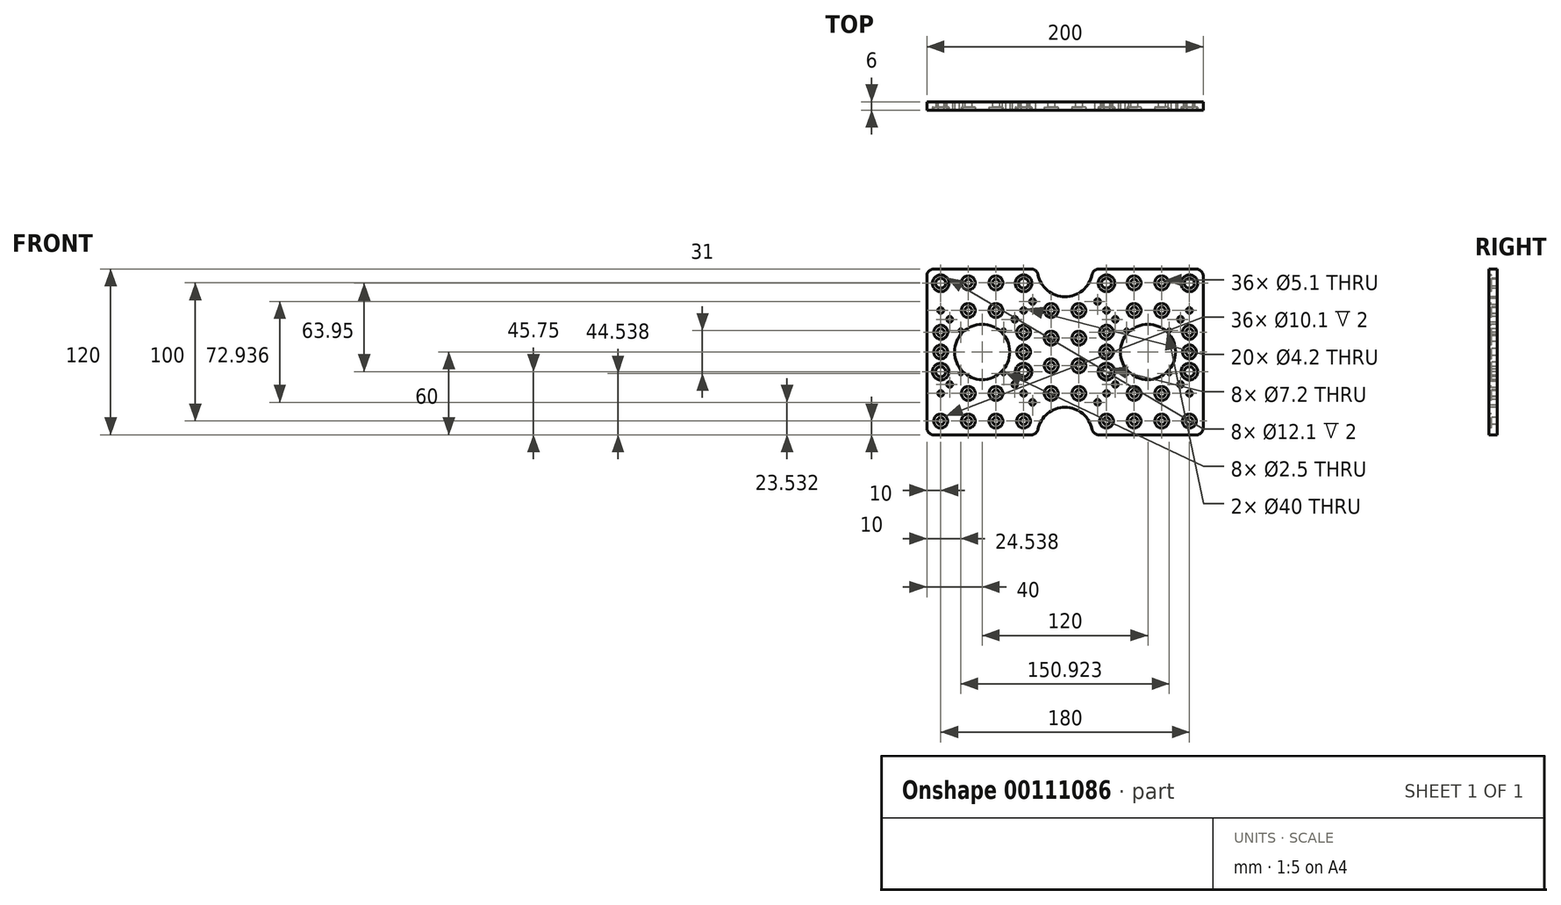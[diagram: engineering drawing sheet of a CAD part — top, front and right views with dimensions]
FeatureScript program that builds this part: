
annotation { "Feature Type Name" : "Feature", "Feature Type Description" : "" }
export const myFeature = defineFeature(function(context is Context, id is Id, definition is map)
    precondition{}
    {
        {
            var Q0;
            Q0=qCreatedBy(makeId("Front.planeOp"),FACE);
            var sketch = newSketch(context, id + "F0", { "sketchPlane" : qUnion([Q0])});
            skPoint(sketch, "E0", {"position": v(10, 10) * mm});
            skPoint(sketch, "E1.0.1.0", {"position": v(10, 30) * mm});
            skPoint(sketch, "E1.1.0.0", {"position": v(30, 10) * mm});
            skPoint(sketch, "E1.1.1.0", {"position": v(30, 30) * mm});
            skPoint(sketch, "E1.2.0.0", {"position": v(50, 10) * mm});
            skPoint(sketch, "E1.2.1.0", {"position": v(50, 30) * mm});
            skPoint(sketch, "E1.3.0.0", {"position": v(70, 10) * mm});
            skPoint(sketch, "E1.3.1.0", {"position": v(70, 30) * mm});
            skLineSegment(sketch, "E1.direction1", {"start": v(10, 10) * mm, "end": v(30, 10) * mm, "construction": true});
            skLineSegment(sketch, "E1.direction2", {"start": v(10, 10) * mm, "end": v(10, 30) * mm, "construction": true});
            skLineSegment(sketch, "E2.bottom", {"start": v(5, 0) * mm, "end": v(75.5, 0) * mm});
            skLineSegment(sketch, "E2.top", {"start": v(5, 120) * mm, "end": v(75.5, 120) * mm});
            skLineSegment(sketch, "E2.left", {"start": v(0, 5) * mm, "end": v(0, 115) * mm});
            skLineSegment(sketch, "E2.right", {"start": v(100, 20) * mm, "end": v(100, 100) * mm});
            skArc(sketch, "E3", {"start": v(80.4, 116) * mm, "mid": v(87.35, 104.5) * mm, "end": v(100, 100) * mm});
            skArc(sketch, "E4", {"start": v(100, 20) * mm, "mid": v(87.35, 15.5) * mm, "end": v(80.4, 4) * mm});
            skCircle(sketch, "E5", {"center": v(40, 60) * mm, "radius": 20 * mm});
            skPoint(sketch, "E5.centerSnap0", {"position": v(0, 60) * mm});
            skPoint(sketch, "E6", {"position": v(10, 60) * mm});
            skPoint(sketch, "E7", {"position": v(70, 60) * mm});
            skPoint(sketch, "E8.0.0.4", {"position": v(10, 90) * mm});
            skPoint(sketch, "E8.0.1.4", {"position": v(30, 90) * mm});
            skPoint(sketch, "E8.0.1.5", {"position": v(30, 110) * mm});
            skPoint(sketch, "E8.0.2.4", {"position": v(50, 90) * mm});
            skPoint(sketch, "E8.0.2.5", {"position": v(50, 110) * mm});
            skPoint(sketch, "E8.0.3.4", {"position": v(70, 90) * mm});
            skPoint(sketch, "E9.0.4.1", {"position": v(90, 30) * mm});
            skPoint(sketch, "E9.0.4.2", {"position": v(90, 50) * mm});
            skPoint(sketch, "E9.0.4.3", {"position": v(90, 70) * mm});
            skPoint(sketch, "E9.0.4.4", {"position": v(90, 90) * mm});
            skPoint(sketch, "E10", {"position": v(24.54, 44.54) * mm});
            skPoint(sketch, "E11.0.1.0", {"position": v(24.54, 75.54) * mm});
            skPoint(sketch, "E11.1.0.0", {"position": v(55.54, 44.54) * mm});
            skPoint(sketch, "E11.1.1.0", {"position": v(55.54, 75.54) * mm});
            skLineSegment(sketch, "E11.direction1", {"start": v(24.54, 44.54) * mm, "end": v(55.54, 44.54) * mm, "construction": true});
            skLineSegment(sketch, "E11.direction2", {"start": v(24.54, 44.54) * mm, "end": v(24.54, 75.54) * mm, "construction": true});
            skPoint(sketch, "E12", {"position": v(16.47, 36.47) * mm});
            skPoint(sketch, "E13.0.1.0", {"position": v(16.47, 83.6) * mm});
            skPoint(sketch, "E13.1.0.0", {"position": v(63.6, 36.47) * mm});
            skPoint(sketch, "E13.1.1.0", {"position": v(63.6, 83.6) * mm});
            skLineSegment(sketch, "E13.direction1", {"start": v(16.47, 36.47) * mm, "end": v(63.6, 36.47) * mm, "construction": true});
            skLineSegment(sketch, "E13.direction2", {"start": v(16.47, 36.47) * mm, "end": v(16.47, 83.6) * mm, "construction": true});
            skPoint(sketch, "E14.visualSharp", {"position": v(0, 120) * mm});
            skArc(sketch, "E14.filletArc", {"start": v(5, 120) * mm, "mid": v(1.46, 118.54) * mm, "end": v(0, 115) * mm});
            skPoint(sketch, "E15.visualSharp", {"position": v(80, 120) * mm});
            skArc(sketch, "E15.filletArc", {"start": v(80.4, 116) * mm, "mid": v(78.67, 118.87) * mm, "end": v(75.5, 120) * mm});
            skPoint(sketch, "E16.visualSharp", {"position": v(0, 0) * mm});
            skArc(sketch, "E16.filletArc", {"start": v(0, 5) * mm, "mid": v(1.46, 1.46) * mm, "end": v(5, 0) * mm});
            skPoint(sketch, "E17.visualSharp", {"position": v(80, 0) * mm});
            skArc(sketch, "E17.filletArc", {"start": v(75.5, 0) * mm, "mid": v(78.67, 1.13) * mm, "end": v(80.4, 4) * mm});
            skPoint(sketch, "E18", {"position": v(10, 45.75) * mm});
            skPoint(sketch, "E19", {"position": v(10, 74.25) * mm});
            skPoint(sketch, "E20", {"position": v(70, 45.75) * mm});
            skPoint(sketch, "E21", {"position": v(70, 74.25) * mm});
            skPoint(sketch, "E22", {"position": v(76.47, 96.47) * mm});
            skPoint(sketch, "E23", {"position": v(76.47, 23.53) * mm});
            skPoint(sketch, "E24", {"position": v(10, 109.7) * mm});
            skPoint(sketch, "E25", {"position": v(70, 109.7) * mm});
            skSolve(sketch);
        }
        {
            var Q0;
            Q0=makeQuery(id+"F0.imprint","IMPRINT",FACE,{"disambiguationData":[TD([[makeQuery(id+"F0.imprint","IMPRINT",EDGE,{"derivedFrom":sQuery(id+"F0.wireOp",EDGE,"E2.bottom")}),1.0]])]});
            extrude(context, id + "F1", {"entities" : qUnion([Q0]), "oppositeDirection" : true, "depth" : 6 * mm});
        }
        {
            var Q0;
            Q0=sQuery(id+"F0.wireOp",VERTEX,"E1.direction2.start");
            var Q1;
            Q1=sQuery(id+"F0.wireOp",VERTEX,"E1.1.0.0");
            var Q2;
            Q2=sQuery(id+"F0.wireOp",VERTEX,"E1.2.0.0");
            var Q3;
            Q3=sQuery(id+"F0.wireOp",VERTEX,"E1.3.0.0");
            var Q4;
            Q4=sQuery(id+"F0.wireOp",VERTEX,"E1.2.1.0");
            var Q5;
            Q5=sQuery(id+"F0.wireOp",VERTEX,"E1.1.1.0");
            var Q6;
            Q6=sQuery(id+"F0.wireOp",VERTEX,"E9.0.4.1");
            var Q7;
            Q7=sQuery(id+"F0.wireOp",VERTEX,"E9.0.4.2");
            var Q8;
            Q8=sQuery(id+"F0.wireOp",VERTEX,"E9.0.4.3");
            var Q9;
            Q9=sQuery(id+"F0.wireOp",VERTEX,"E9.0.4.4");
            var Q10;
            Q10=sQuery(id+"F0.wireOp",VERTEX,"E8.0.2.4");
            var Q11;
            Q11=sQuery(id+"F0.wireOp",VERTEX,"E8.0.2.5");
            var Q12;
            Q12=sQuery(id+"F0.wireOp",VERTEX,"E8.0.1.5");
            var Q13;
            Q13=sQuery(id+"F0.wireOp",VERTEX,"E8.0.1.4");
            var Q14;
            Q14=sQuery(id+"F0.wireOp",VERTEX,"E7");
            var Q15;
            Q15=sQuery(id+"F0.wireOp",VERTEX,"E6");
            var Q16;
            Q16=sQuery(id+"F0.wireOp",VERTEX,"E21");
            var Q17;
            Q17=sQuery(id+"F0.wireOp",VERTEX,"E19");
            var Q18;
            Q18=makeQuery(id+"F1.opExtrude","SWEPT_BODY",BODY,{"disambiguationData":[OSD([sQuery(id+"F0.wireOp",EDGE,"E2.bottom"),sQuery(id+"F0.wireOp",EDGE,"E2.top"),sQuery(id+"F0.wireOp",EDGE,"E2.left"),sQuery(id+"F0.wireOp",EDGE,"E2.right"),sQuery(id+"F0.wireOp",EDGE,"E3"),sQuery(id+"F0.wireOp",EDGE,"E4"),sQuery(id+"F0.wireOp",EDGE,"E5"),sQuery(id+"F0.wireOp",EDGE,"E14.filletArc"),sQuery(id+"F0.wireOp",EDGE,"E15.filletArc"),sQuery(id+"F0.wireOp",EDGE,"E16.filletArc"),sQuery(id+"F0.wireOp",EDGE,"E17.filletArc")])]});
            hole(context, id + "F2", {"style" : HoleStyle.C_BORE, "endStyle" : HoleEndStyle.THROUGH, "standardTappedOrClearance" : lookupTablePath({ "standard" : "ISO", "fit" : "Close", "size" : "5.1", "type" : "Drilled" }), "standardBlindInLast" : lookupTablePath({ "fit" : "Close", "standard" : "ISO", "size" : "5.1", "type" : "Drilled" }), "holeDiameter" : 5.1 * mm, "cBoreDiameter" : 10.1 * mm, "cBoreDepth" : 2 * mm, "locations" : qUnion([Q0, Q1, Q2, Q3, Q4, Q5, Q6, Q7, Q8, Q9, Q10, Q11, Q12, Q13, Q14, Q15, Q16, Q17]), "scope" : qUnion([Q18]), "isTappedThrough" : true});
        }
        {
            var Q0;
            Q0=sQuery(id+"F0.wireOp",VERTEX,"E24");
            var Q1;
            Q1=sQuery(id+"F0.wireOp",VERTEX,"E25");
            var Q2;
            Q2=sQuery(id+"F0.wireOp",VERTEX,"E18");
            var Q3;
            Q3=sQuery(id+"F0.wireOp",VERTEX,"E20");
            var Q4;
            Q4=makeQuery(id+"F1.opExtrude","SWEPT_BODY",BODY,{"disambiguationData":[OSD([sQuery(id+"F0.wireOp",EDGE,"E2.bottom"),sQuery(id+"F0.wireOp",EDGE,"E2.top"),sQuery(id+"F0.wireOp",EDGE,"E2.left"),sQuery(id+"F0.wireOp",EDGE,"E2.right"),sQuery(id+"F0.wireOp",EDGE,"E3"),sQuery(id+"F0.wireOp",EDGE,"E4"),sQuery(id+"F0.wireOp",EDGE,"E5"),sQuery(id+"F0.wireOp",EDGE,"E14.filletArc"),sQuery(id+"F0.wireOp",EDGE,"E15.filletArc"),sQuery(id+"F0.wireOp",EDGE,"E16.filletArc"),sQuery(id+"F0.wireOp",EDGE,"E17.filletArc")])]});
            hole(context, id + "F3", {"style" : HoleStyle.C_BORE, "endStyle" : HoleEndStyle.THROUGH, "holeDiameter" : 7.2 * mm, "cBoreDiameter" : 12.1 * mm, "cBoreDepth" : 2 * mm, "locations" : qUnion([Q0, Q1, Q2, Q3]), "scope" : qUnion([Q4]), "isTappedThrough" : true});
        }
        {
            var Q0;
            Q0=sQuery(id+"F0.wireOp",VERTEX,"E12");
            var Q1;
            Q1=sQuery(id+"F0.wireOp",VERTEX,"E1.0.1.0");
            var Q2;
            Q2=sQuery(id+"F0.wireOp",VERTEX,"E13.0.1.0");
            var Q3;
            Q3=sQuery(id+"F0.wireOp",VERTEX,"E8.0.0.4");
            var Q4;
            Q4=sQuery(id+"F0.wireOp",VERTEX,"E13.1.1.0");
            var Q5;
            Q5=sQuery(id+"F0.wireOp",VERTEX,"E8.0.3.4");
            var Q6;
            Q6=sQuery(id+"F0.wireOp",VERTEX,"E22");
            var Q7;
            Q7=sQuery(id+"F0.wireOp",VERTEX,"E23");
            var Q8;
            Q8=sQuery(id+"F0.wireOp",VERTEX,"E1.3.1.0");
            var Q9;
            Q9=sQuery(id+"F0.wireOp",VERTEX,"E13.1.0.0");
            var Q10;
            Q10=makeQuery(id+"F1.opExtrude","SWEPT_BODY",BODY,{"disambiguationData":[OSD([sQuery(id+"F0.wireOp",EDGE,"E2.bottom"),sQuery(id+"F0.wireOp",EDGE,"E2.top"),sQuery(id+"F0.wireOp",EDGE,"E2.left"),sQuery(id+"F0.wireOp",EDGE,"E2.right"),sQuery(id+"F0.wireOp",EDGE,"E3"),sQuery(id+"F0.wireOp",EDGE,"E4"),sQuery(id+"F0.wireOp",EDGE,"E5"),sQuery(id+"F0.wireOp",EDGE,"E14.filletArc"),sQuery(id+"F0.wireOp",EDGE,"E15.filletArc"),sQuery(id+"F0.wireOp",EDGE,"E16.filletArc"),sQuery(id+"F0.wireOp",EDGE,"E17.filletArc")])]});
            hole(context, id + "F4", {"style" : HoleStyle.SIMPLE, "endStyle" : HoleEndStyle.THROUGH, "standardTappedOrClearance" : lookupTablePath({ "standard" : "ISO", "fit" : "Normal", "engagement" : "75%", "pitch" : "0.8 mm", "size" : "M5", "type" : "Tapped" }), "standardBlindInLast" : lookupTablePath({ "fit" : "Standard", "standard" : "ISO", "engagement" : "75%", "pitch" : "0.8 mm", "size" : "M5", "type" : "Tapped" }), "holeDiameter" : 4.2 * mm, "locations" : qUnion([Q0, Q1, Q2, Q3, Q4, Q5, Q6, Q7, Q8, Q9]), "scope" : qUnion([Q10]), "isTappedThrough" : true, "majorDiameter" : 5 * mm, "showTappedDepth" : true});
        }
        {
            var Q0;
            Q0=sQuery(id+"F0.wireOp",VERTEX,"E11.1.0.0");
            var Q1;
            Q1=sQuery(id+"F0.wireOp",VERTEX,"E11.1.1.0");
            var Q2;
            Q2=sQuery(id+"F0.wireOp",VERTEX,"E11.0.1.0");
            var Q3;
            Q3=sQuery(id+"F0.wireOp",VERTEX,"E10");
            var Q4;
            Q4=makeQuery(id+"F1.opExtrude","SWEPT_BODY",BODY,{"disambiguationData":[OSD([sQuery(id+"F0.wireOp",EDGE,"E2.bottom"),sQuery(id+"F0.wireOp",EDGE,"E2.top"),sQuery(id+"F0.wireOp",EDGE,"E2.left"),sQuery(id+"F0.wireOp",EDGE,"E2.right"),sQuery(id+"F0.wireOp",EDGE,"E3"),sQuery(id+"F0.wireOp",EDGE,"E4"),sQuery(id+"F0.wireOp",EDGE,"E5"),sQuery(id+"F0.wireOp",EDGE,"E14.filletArc"),sQuery(id+"F0.wireOp",EDGE,"E15.filletArc"),sQuery(id+"F0.wireOp",EDGE,"E16.filletArc"),sQuery(id+"F0.wireOp",EDGE,"E17.filletArc")])]});
            hole(context, id + "F5", {"style" : HoleStyle.SIMPLE, "endStyle" : HoleEndStyle.THROUGH, "standardTappedOrClearance" : lookupTablePath({ "standard" : "ISO", "fit" : "Normal", "engagement" : "75%", "pitch" : "0.5 mm", "size" : "M3", "type" : "Tapped" }), "standardBlindInLast" : lookupTablePath({ "fit" : "Standard", "standard" : "ISO", "engagement" : "75%", "pitch" : "0.5 mm", "size" : "M3", "type" : "Tapped" }), "holeDiameter" : 2.5 * mm, "locations" : qUnion([Q0, Q1, Q2, Q3]), "scope" : qUnion([Q4]), "isTappedThrough" : true, "majorDiameter" : 3 * mm, "showTappedDepth" : true});
        }
        {
            var Q0;
            Q0=makeQuery(id+"F1.opExtrude","SWEPT_BODY",BODY,{"disambiguationData":[OSD([sQuery(id+"F0.wireOp",EDGE,"E2.bottom"),sQuery(id+"F0.wireOp",EDGE,"E2.top"),sQuery(id+"F0.wireOp",EDGE,"E2.left"),sQuery(id+"F0.wireOp",EDGE,"E2.right"),sQuery(id+"F0.wireOp",EDGE,"E3"),sQuery(id+"F0.wireOp",EDGE,"E4"),sQuery(id+"F0.wireOp",EDGE,"E5"),sQuery(id+"F0.wireOp",EDGE,"E14.filletArc"),sQuery(id+"F0.wireOp",EDGE,"E15.filletArc"),sQuery(id+"F0.wireOp",EDGE,"E16.filletArc"),sQuery(id+"F0.wireOp",EDGE,"E17.filletArc")])]});
            var Q1;
            Q1=makeQuery(id+"F1.opExtrude","SWEPT_FACE",FACE,{"disambiguationData":[OSD([sQuery(id+"F0.wireOp",EDGE,"E2.right")])]});
            mirror(context, id + "F6", {"operationType" : NewBodyOperationType.ADD, "entities" : qUnion([Q0]), "mirrorPlane" : qUnion([Q1])});
        }
    });
